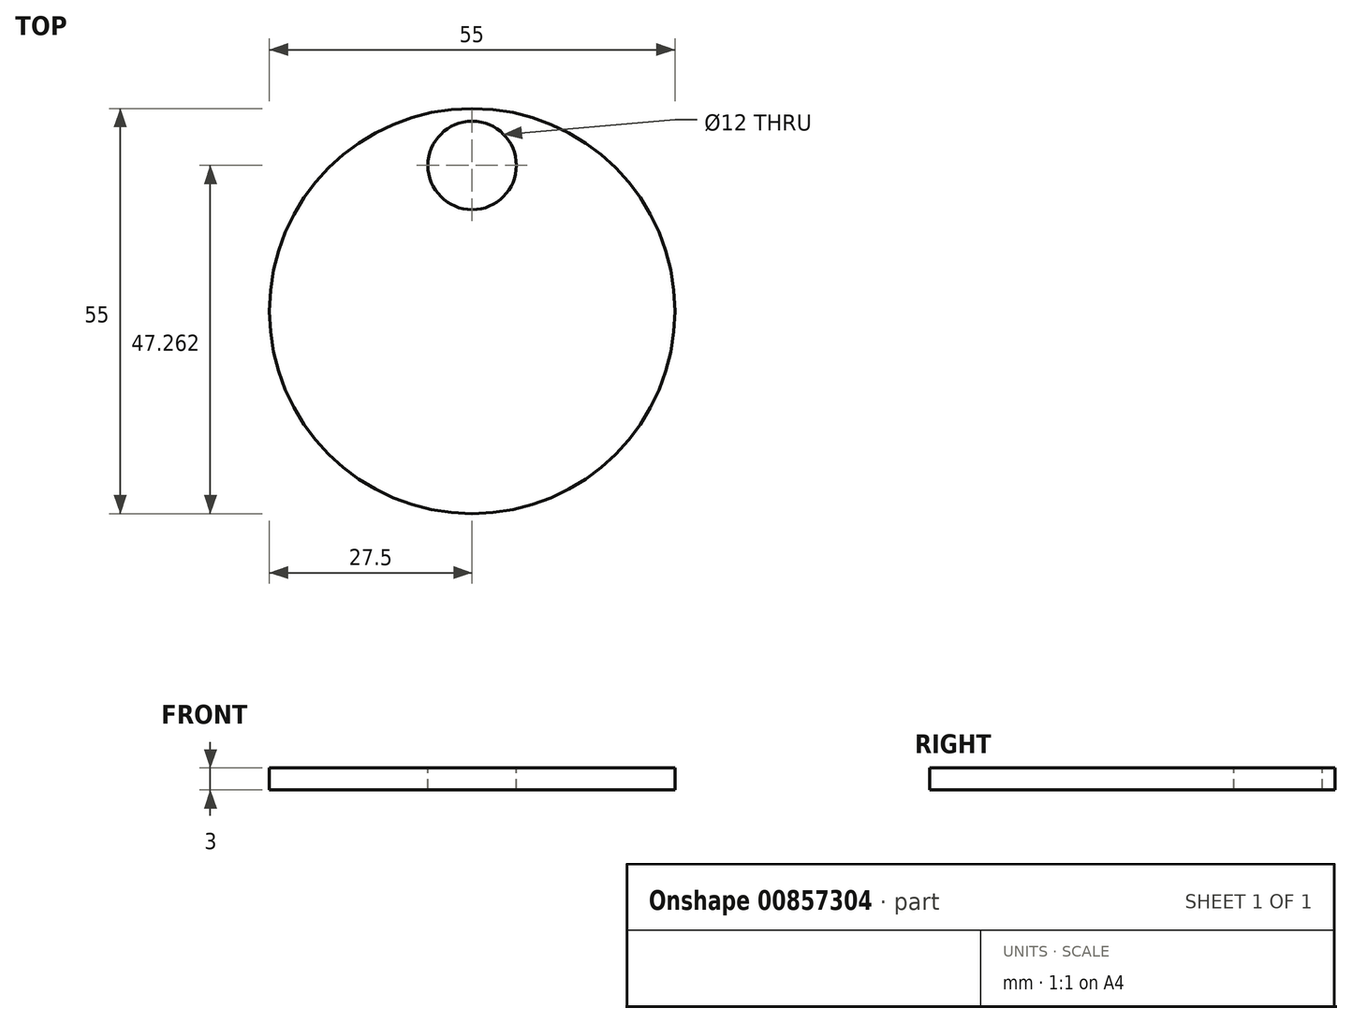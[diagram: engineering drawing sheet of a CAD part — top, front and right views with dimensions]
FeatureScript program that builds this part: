
annotation { "Feature Type Name" : "Feature", "Feature Type Description" : "" }
export const myFeature = defineFeature(function(context is Context, id is Id, definition is map)
    precondition{}
    {
        {
            var Q0;
            Q0=qCreatedBy(makeId("Top.planeOp"),FACE);
            var sketch = newSketch(context, id + "F0", { "sketchPlane" : qUnion([Q0])});
            skCircle(sketch, "E0", {"center": v(0, 0) * mm, "radius": 27.5 * mm});
            skSolve(sketch);
        }
        {
            var Q0;
            Q0 = qSketchRegion(id + "F0", true);
            extrude(context, id + "F1", {"entities" : qUnion([Q0]), "depth" : 3 * mm, "offsetDistance" : 25 * mm});
        }
        {
            var Q0;
            Q0=makeQuery(id+"F1.opExtrude","CAP_FACE",FACE,{"disambiguationData":[OSD([sQuery(id+"F0.wireOp",EDGE,"E0")])],"isStart":false});
            var sketch = newSketch(context, id + "F2", { "sketchPlane" : qUnion([Q0])});
            skLineSegment(sketch, "E1", {"start": v(0, 0) * mm, "end": v(0, 27.5) * mm, "construction": true});
            skCircle(sketch, "E2", {"center": v(0, 19.76) * mm, "radius": 6 * mm});
            skSolve(sketch);
        }
        {
            var Q0;
            Q0 = qSketchRegion(id + "F2", true);
            extrude(context, id + "F3", {"entities" : qUnion([Q0]), "operationType" : NewBodyOperationType.REMOVE, "endBound" : BoundingType.THROUGH_ALL, "oppositeDirection" : true, "depth" : 25 * mm, "offsetDistance" : 25 * mm});
        }
    });
